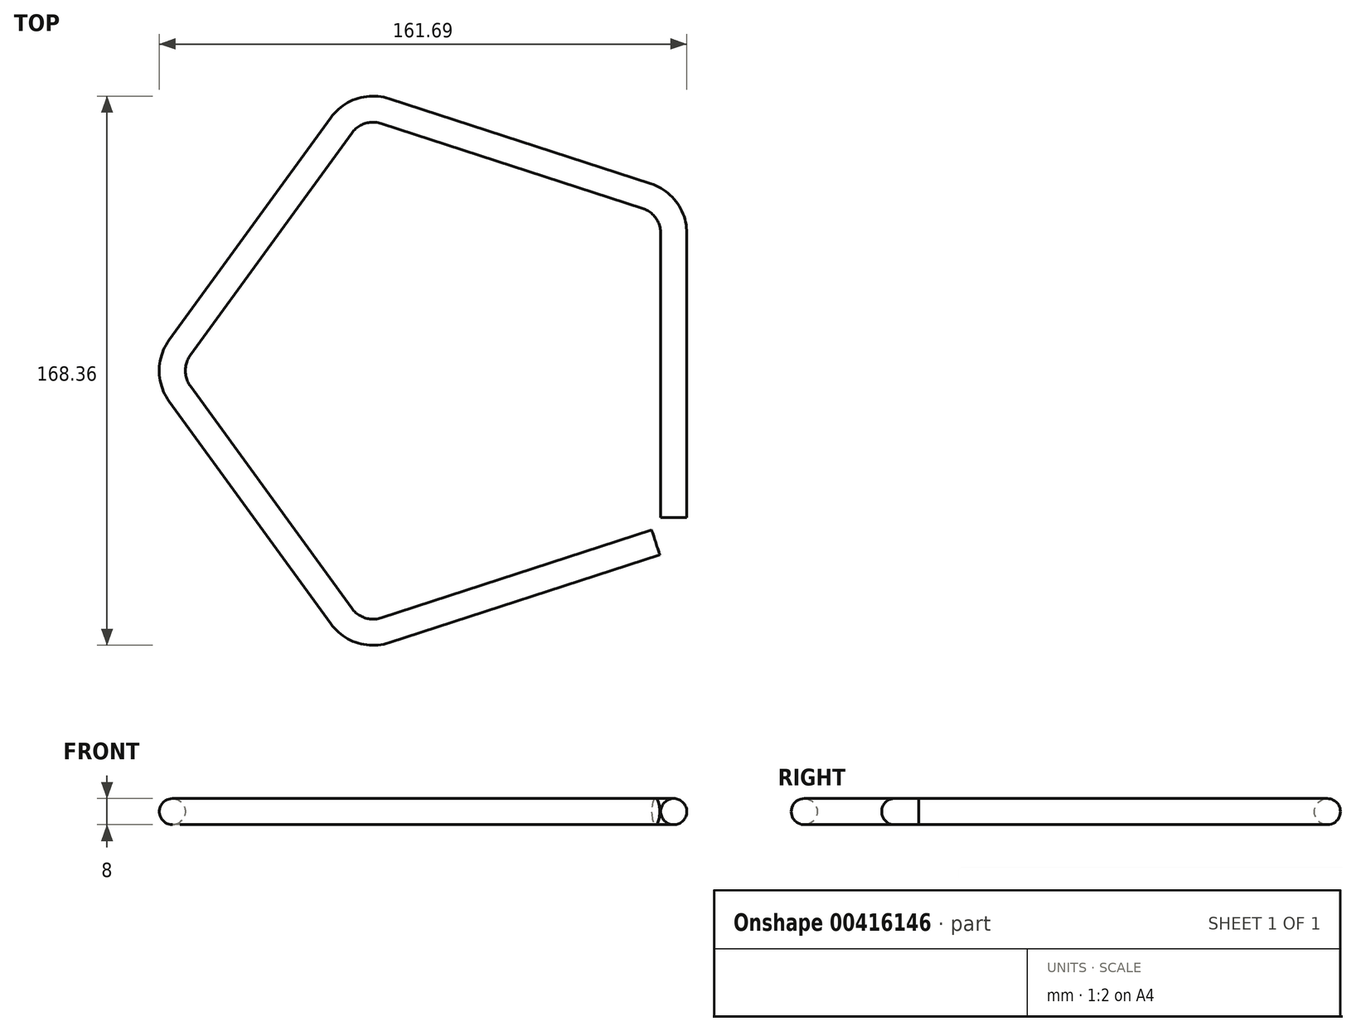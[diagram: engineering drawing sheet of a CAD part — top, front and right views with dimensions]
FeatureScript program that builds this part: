
annotation { "Feature Type Name" : "Feature", "Feature Type Description" : "" }
export const myFeature = defineFeature(function(context is Context, id is Id, definition is map)
    precondition{}
    {
        {
            var Q0;
            Q0=qCreatedBy(makeId("Top.planeOp"),FACE);
            var sketch = newSketch(context, id + "F0", { "sketchPlane" : qUnion([Q0])});
            skCircle(sketch, "E0.cCircle", {"center": v(0, 0) * mm, "radius": 70 * mm, "construction": true});
            skLineSegment(sketch, "E0.0", {"start": v(70, 42.14) * mm, "end": v(70, -45.05) * mm});
            skLineSegment(sketch, "E0.1", {"start": v(64.47, -52.65) * mm, "end": v(-18.45, -79.6) * mm});
            skLineSegment(sketch, "E0.2", {"start": v(-31.86, -75.24) * mm, "end": v(-81.4, -7.05) * mm});
            skLineSegment(sketch, "E0.3", {"start": v(-81.4, 7.05) * mm, "end": v(-31.86, 75.24) * mm});
            skLineSegment(sketch, "E0.4", {"start": v(-18.45, 79.6) * mm, "end": v(61.7, 53.55) * mm});
            skPoint(sketch, "E0.0.midPoint", {"position": v(70, 0) * mm});
            skPoint(sketch, "E1.visualSharp", {"position": v(-26.74, 82.29) * mm});
            skArc(sketch, "E1.filletArc", {"start": v(-18.45, 79.6) * mm, "mid": v(-25.86, 79.6) * mm, "end": v(-31.86, 75.24) * mm});
            skPoint(sketch, "E2.visualSharp", {"position": v(70, 50.86) * mm});
            skArc(sketch, "E2.filletArc", {"start": v(70, 42.14) * mm, "mid": v(67.7, 49.2) * mm, "end": v(61.7, 53.55) * mm});
            skPoint(sketch, "E3.visualSharp", {"position": v(70, -50.86) * mm});
            skPoint(sketch, "E4.visualSharp", {"position": v(-26.74, -82.29) * mm});
            skArc(sketch, "E4.filletArc", {"start": v(-31.86, -75.24) * mm, "mid": v(-25.86, -79.6) * mm, "end": v(-18.45, -79.6) * mm});
            skPoint(sketch, "E5.visualSharp", {"position": v(-86.52, 0) * mm});
            skArc(sketch, "E5.filletArc", {"start": v(-81.4, 7.05) * mm, "mid": v(-83.7, 0) * mm, "end": v(-81.4, -7.05) * mm});
            skSolve(sketch);
        }
        {
            var Q0;
            Q0=qCreatedBy(makeId("Front.planeOp"),FACE);
            var sketch = newSketch(context, id + "F1", { "sketchPlane" : qUnion([Q0])});
            skCircle(sketch, "E6", {"center": v(70, 0) * mm, "radius": 4 * mm});
            skSolve(sketch);
        }
        {
            var Q0;
            Q0=makeQuery(id+"F1.imprint","IMPRINT",FACE,{"disambiguationData":[TD([[makeQuery(id+"F1.imprint","IMPRINT",EDGE,{"derivedFrom":sQuery(id+"F1.wireOp",EDGE,"E6")}),1.0]])]});
            var Q1;
            Q1 = qConstructionFilter(qBodyType(qCreatedBy(id + "F0" ,EDGE), BodyType.WIRE), ConstructionObject.NO);
            sweep(context, id + "F2", {"profiles" : qUnion([Q0]), "path" : qUnion([Q1])});
        }
    });
